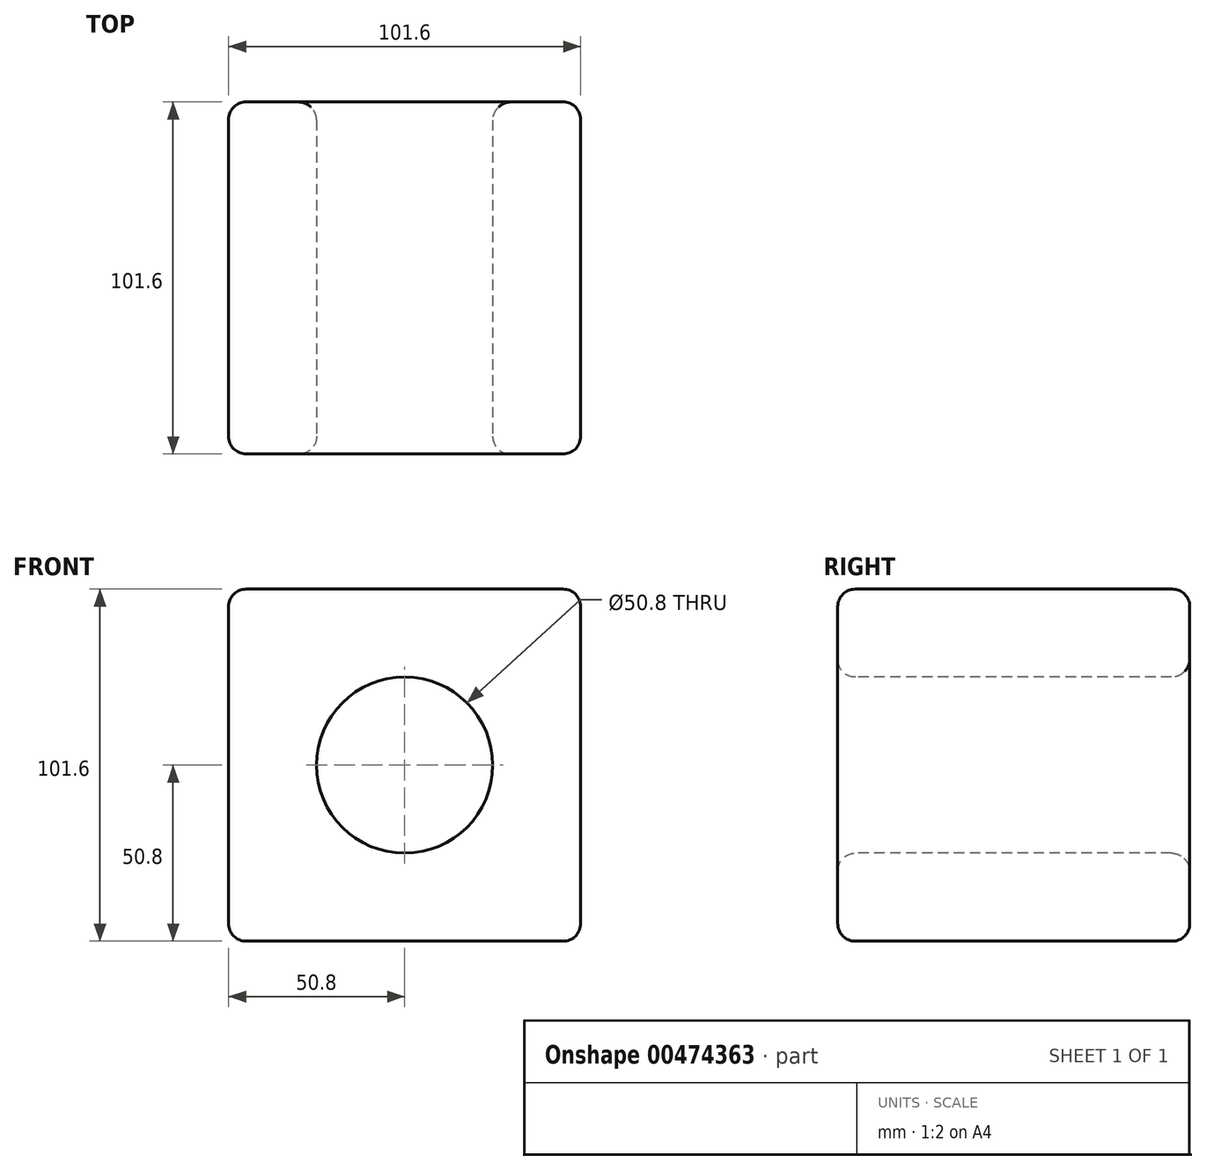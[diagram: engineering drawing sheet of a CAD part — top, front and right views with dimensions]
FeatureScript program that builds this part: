
annotation { "Feature Type Name" : "Feature", "Feature Type Description" : "" }
export const myFeature = defineFeature(function(context is Context, id is Id, definition is map)
    precondition{}
    {
        {
            var Q0;
            Q0=qCreatedBy(makeId("Front.planeOp"),FACE);
            var sketch = newSketch(context, id + "F0", { "sketchPlane" : qUnion([Q0])});
            skLineSegment(sketch, "E0.bottom", {"start": v(-50.8, 50.8) * mm, "end": v(50.8, 50.8) * mm});
            skLineSegment(sketch, "E0.top", {"start": v(-50.8, -50.8) * mm, "end": v(50.8, -50.8) * mm});
            skLineSegment(sketch, "E0.left", {"start": v(-50.8, 50.8) * mm, "end": v(-50.8, -50.8) * mm});
            skLineSegment(sketch, "E0.right", {"start": v(50.8, 50.8) * mm, "end": v(50.8, -50.8) * mm});
            skLineSegment(sketch, "E1", {"start": v(-50.8, 50.8) * mm, "end": v(50.8, -50.8) * mm, "construction": true});
            skSolve(sketch);
        }
        {
            var Q0;
            Q0 = qSketchRegion(id + "F0", true);
            extrude(context, id + "F1", {"entities" : qUnion([Q0]), "endBound" : BoundingType.SYMMETRIC, "depth" : 101.6 * mm});
        }
        {
            var Q0;
            Q0=makeQuery(id+"F1.opExtrude","CAP_FACE",FACE,{"disambiguationData":[OSD([sQuery(id+"F0.wireOp",EDGE,"E0.bottom"),sQuery(id+"F0.wireOp",EDGE,"E0.top"),sQuery(id+"F0.wireOp",EDGE,"E0.left"),sQuery(id+"F0.wireOp",EDGE,"E0.right")])],"isStart":false});
            var sketch = newSketch(context, id + "F2", { "sketchPlane" : qUnion([Q0])});
            skCircle(sketch, "E2", {"center": v(0, 0) * mm, "radius": 25.4 * mm});
            skSolve(sketch);
        }
        {
            var Q0;
            Q0 = qSketchRegion(id + "F2", true);
            extrude(context, id + "F3", {"entities" : qUnion([Q0]), "operationType" : NewBodyOperationType.REMOVE, "endBound" : BoundingType.THROUGH_ALL, "oppositeDirection" : true, "depth" : 25.4 * mm});
        }
        {
            var Q0;
            Q0=makeQuery(id+"F3.boolean.opBoolean","COPY",EDGE,{"derivedFrom":makeQuery(id+"F3.opExtrude","CAP_EDGE",EDGE,{"disambiguationData":[OSD([sQuery(id+"F2.wireOp",EDGE,"E2")])],"isStart":true})});
            var Q1;
            Q1=makeQuery(id+"F3.boolean.opBoolean","INTERSECT",EDGE,{"derivedFrom":[makeQuery(id+"F1.opExtrude","CAP_FACE",FACE,{"disambiguationData":[OSD([sQuery(id+"F0.wireOp",EDGE,"E0.bottom"),sQuery(id+"F0.wireOp",EDGE,"E0.top"),sQuery(id+"F0.wireOp",EDGE,"E0.left"),sQuery(id+"F0.wireOp",EDGE,"E0.right")])],"isStart":true}),makeQuery(id+"F3.opExtrude","SWEPT_FACE",FACE,{"disambiguationData":[OSD([sQuery(id+"F2.wireOp",EDGE,"E2")])]})]});
            chamfer(context, id + "F4", {"entities" : qUnion([Q0, Q1]), "width" : 3.17 * mm, "tangentPropagation" : true});
        }
        {
            var Q0;
            Q0=makeQuery(id+"F1.opExtrude","SWEPT_EDGE",EDGE,{"disambiguationData":[OSD([sQuery(id+"F0.wireOp",EDGE,"E0.top"),sQuery(id+"F0.wireOp",EDGE,"E0.right")])]});
            var Q1;
            Q1=makeQuery(id+"F1.opExtrude","SWEPT_EDGE",EDGE,{"disambiguationData":[OSD([sQuery(id+"F0.wireOp",EDGE,"E0.bottom"),sQuery(id+"F0.wireOp",EDGE,"E0.right")])]});
            var Q2;
            Q2=makeQuery(id+"F1.opExtrude","SWEPT_FACE",FACE,{"disambiguationData":[OSD([sQuery(id+"F0.wireOp",EDGE,"E0.bottom")])]});
            var Q3;
            Q3=makeQuery(id+"F1.opExtrude","SWEPT_FACE",FACE,{"disambiguationData":[OSD([sQuery(id+"F0.wireOp",EDGE,"E0.top")])]});
            var Q4;
            Q4=makeQuery(id+"F1.opExtrude","SWEPT_FACE",FACE,{"disambiguationData":[OSD([sQuery(id+"F0.wireOp",EDGE,"E0.left")])]});
            var Q5;
            Q5=makeQuery(id+"F1.opExtrude","CAP_EDGE",EDGE,{"disambiguationData":[OSD([sQuery(id+"F0.wireOp",EDGE,"E0.bottom")])],"isStart":true});
            var Q6;
            Q6=makeQuery(id+"F1.opExtrude","SWEPT_EDGE",EDGE,{"disambiguationData":[OSD([sQuery(id+"F0.wireOp",EDGE,"E0.bottom"),sQuery(id+"F0.wireOp",EDGE,"E0.left")])]});
            var Q7;
            Q7=makeQuery(id+"F1.opExtrude","CAP_EDGE",EDGE,{"disambiguationData":[OSD([sQuery(id+"F0.wireOp",EDGE,"E0.bottom")])],"isStart":false});
            var Q8;
            Q8=makeQuery(id+"F1.opExtrude","SWEPT_FACE",FACE,{"disambiguationData":[OSD([sQuery(id+"F0.wireOp",EDGE,"E0.right")])]});
            var Q9;
            Q9=makeQuery(id+"F1.opExtrude","CAP_EDGE",EDGE,{"disambiguationData":[OSD([sQuery(id+"F0.wireOp",EDGE,"E0.top")])],"isStart":true});
            var Q10;
            Q10=makeQuery(id+"F4.opChamfer","BLEND_FACE",FACE,{"disambiguationData":[OSD([sQuery(id+"F0.wireOp",EDGE,"E0.bottom"),sQuery(id+"F0.wireOp",EDGE,"E0.top"),sQuery(id+"F0.wireOp",EDGE,"E0.left"),sQuery(id+"F0.wireOp",EDGE,"E0.right"),sQuery(id+"F2.wireOp",EDGE,"E2")])]});
            var Q11;
            {var subQ0=makeQuery(id+"F1.opExtrude","CAP_FACE",FACE,{"disambiguationData":[OSD([sQuery(id+"F0.wireOp",EDGE,"E0.bottom"),sQuery(id+"F0.wireOp",EDGE,"E0.top"),sQuery(id+"F0.wireOp",EDGE,"E0.left"),sQuery(id+"F0.wireOp",EDGE,"E0.right")])],"isStart":true});Q11=makeQuery(id+"F4.opChamfer","BLEND_EDGE",EDGE,{"blendedFrom":[makeQuery(id+"F3.boolean.opBoolean","INTERSECT",EDGE,{"derivedFrom":[subQ0,makeQuery(id+"F3.opExtrude","SWEPT_FACE",FACE,{"disambiguationData":[OSD([sQuery(id+"F2.wireOp",EDGE,"E2")])]})]}),subQ0],"blendedInto":[subQ0]});}
            var Q12;
            {var subQ0=makeQuery(id+"F3.opExtrude","SWEPT_FACE",FACE,{"disambiguationData":[OSD([sQuery(id+"F2.wireOp",EDGE,"E2")])]});Q12=makeQuery(id+"F4.opChamfer","BLEND_EDGE",EDGE,{"blendedFrom":[makeQuery(id+"F3.boolean.opBoolean","INTERSECT",EDGE,{"derivedFrom":[makeQuery(id+"F1.opExtrude","CAP_FACE",FACE,{"disambiguationData":[OSD([sQuery(id+"F0.wireOp",EDGE,"E0.bottom"),sQuery(id+"F0.wireOp",EDGE,"E0.top"),sQuery(id+"F0.wireOp",EDGE,"E0.left"),sQuery(id+"F0.wireOp",EDGE,"E0.right")])],"isStart":true}),subQ0]}),makeQuery(id+"F3.boolean.opBoolean","COPY",FACE,{"derivedFrom":subQ0})],"blendedInto":[makeQuery(id+"F3.boolean.opBoolean","COPY",FACE,{"derivedFrom":subQ0})]});}
            var Q13;
            Q13=makeQuery(id+"F3.boolean.opBoolean","COPY",FACE,{"derivedFrom":makeQuery(id+"F3.opExtrude","SWEPT_FACE",FACE,{"disambiguationData":[OSD([sQuery(id+"F2.wireOp",EDGE,"E2")])]})});
            var Q14;
            Q14=makeQuery(id+"F1.opExtrude","CAP_FACE",FACE,{"disambiguationData":[OSD([sQuery(id+"F0.wireOp",EDGE,"E0.bottom"),sQuery(id+"F0.wireOp",EDGE,"E0.top"),sQuery(id+"F0.wireOp",EDGE,"E0.left"),sQuery(id+"F0.wireOp",EDGE,"E0.right")])],"isStart":true});
            var Q15;
            Q15=makeQuery(id+"F4.opChamfer","BLEND_FACE",FACE,{"disambiguationData":[OSD([sQuery(id+"F2.wireOp",EDGE,"E2")])]});
            var Q16;
            {var subQ0=sQuery(id+"F2.wireOp",EDGE,"E2");Q16=makeQuery(id+"F4.opChamfer","BLEND_EDGE",EDGE,{"blendedFrom":[makeQuery(id+"F3.boolean.opBoolean","COPY",EDGE,{"derivedFrom":makeQuery(id+"F3.opExtrude","CAP_EDGE",EDGE,{"disambiguationData":[OSD([subQ0])],"isStart":true})}),makeQuery(id+"F3.boolean.opBoolean","COPY",FACE,{"derivedFrom":makeQuery(id+"F3.opExtrude","SWEPT_FACE",FACE,{"disambiguationData":[OSD([subQ0])]})})],"blendedInto":[makeQuery(id+"F3.boolean.opBoolean","COPY",FACE,{"derivedFrom":makeQuery(id+"F3.opExtrude","SWEPT_FACE",FACE,{"disambiguationData":[OSD([subQ0])]})})]});}
            var Q17;
            Q17=makeQuery(id+"F1.opExtrude","SWEPT_EDGE",EDGE,{"disambiguationData":[OSD([sQuery(id+"F0.wireOp",EDGE,"E0.top"),sQuery(id+"F0.wireOp",EDGE,"E0.left")])]});
            var Q18;
            Q18=makeQuery(id+"F1.opExtrude","CAP_EDGE",EDGE,{"disambiguationData":[OSD([sQuery(id+"F0.wireOp",EDGE,"E0.top")])],"isStart":false});
            var Q19;
            Q19=makeQuery(id+"F1.opExtrude","CAP_EDGE",EDGE,{"disambiguationData":[OSD([sQuery(id+"F0.wireOp",EDGE,"E0.left")])],"isStart":true});
            var Q20;
            Q20=makeQuery(id+"F1.opExtrude","CAP_EDGE",EDGE,{"disambiguationData":[OSD([sQuery(id+"F0.wireOp",EDGE,"E0.left")])],"isStart":false});
            var Q21;
            Q21=makeQuery(id+"F1.opExtrude","CAP_EDGE",EDGE,{"disambiguationData":[OSD([sQuery(id+"F0.wireOp",EDGE,"E0.right")])],"isStart":true});
            var Q22;
            Q22=makeQuery(id+"F1.opExtrude","CAP_EDGE",EDGE,{"disambiguationData":[OSD([sQuery(id+"F0.wireOp",EDGE,"E0.right")])],"isStart":false});
            var Q23;
            Q23=makeQuery(id+"F4.opChamfer","BLEND_EDGE",EDGE,{"blendedFrom":[makeQuery(id+"F3.boolean.opBoolean","COPY",EDGE,{"derivedFrom":makeQuery(id+"F3.opExtrude","CAP_EDGE",EDGE,{"disambiguationData":[OSD([sQuery(id+"F2.wireOp",EDGE,"E2")])],"isStart":true})}),makeQuery(id+"F1.opExtrude","CAP_FACE",FACE,{"disambiguationData":[OSD([sQuery(id+"F0.wireOp",EDGE,"E0.bottom"),sQuery(id+"F0.wireOp",EDGE,"E0.top"),sQuery(id+"F0.wireOp",EDGE,"E0.left"),sQuery(id+"F0.wireOp",EDGE,"E0.right")])],"isStart":false})],"blendedInto":[makeQuery(id+"F1.opExtrude","CAP_FACE",FACE,{"disambiguationData":[OSD([sQuery(id+"F0.wireOp",EDGE,"E0.bottom"),sQuery(id+"F0.wireOp",EDGE,"E0.top"),sQuery(id+"F0.wireOp",EDGE,"E0.left"),sQuery(id+"F0.wireOp",EDGE,"E0.right")])],"isStart":false})]});
            var Q24;
            Q24=makeQuery(id+"F1.opExtrude","CAP_FACE",FACE,{"disambiguationData":[OSD([sQuery(id+"F0.wireOp",EDGE,"E0.bottom"),sQuery(id+"F0.wireOp",EDGE,"E0.top"),sQuery(id+"F0.wireOp",EDGE,"E0.left"),sQuery(id+"F0.wireOp",EDGE,"E0.right")])],"isStart":false});
            fillet(context, id + "F5", {"entities" : qUnion([Q0, Q1, Q2, Q3, Q4, Q5, Q6, Q7, Q8, Q9, Q10, Q11, Q12, Q13, Q14, Q15, Q16, Q17, Q18, Q19, Q20, Q21, Q22, Q23, Q24]), "radius" : 5.08 * mm, "tangentPropagation" : true, "allowEdgeOverflow" : false});
        }
    });
